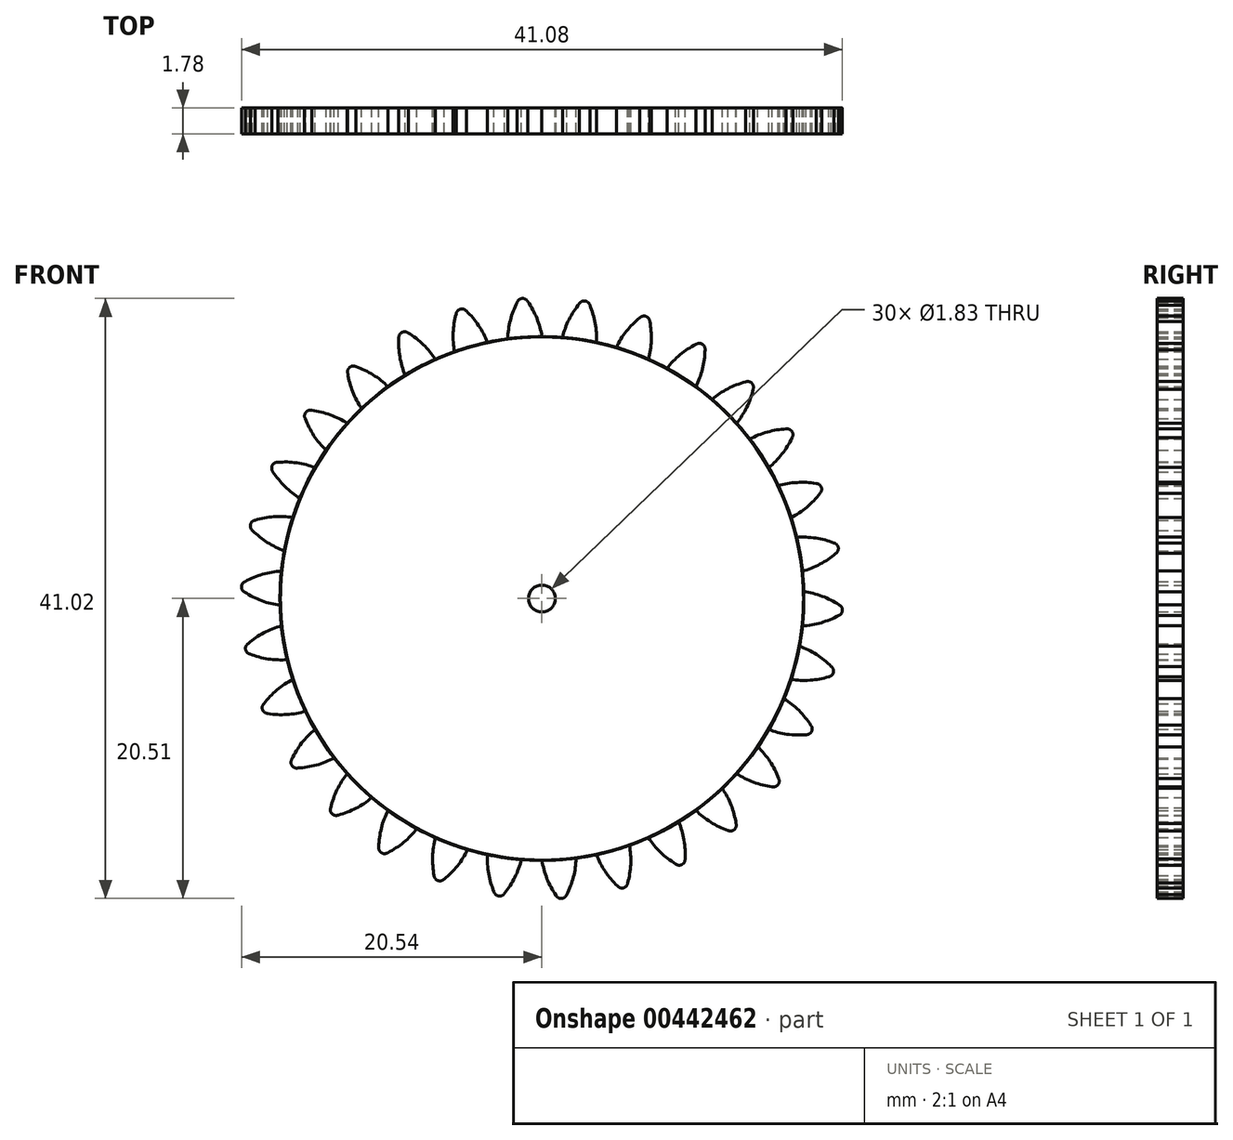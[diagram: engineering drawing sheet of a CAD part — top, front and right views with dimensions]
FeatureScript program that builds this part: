
annotation { "Feature Type Name" : "Feature", "Feature Type Description" : "" }
export const myFeature = defineFeature(function(context is Context, id is Id, definition is map)
    precondition{}
    {
        {
            var Q0;
            Q0=qCreatedBy(makeId("Front.planeOp"),FACE);
            var sketch = newSketch(context, id + "F0", { "sketchPlane" : qUnion([Q0])});
            skCircle(sketch, "E0", {"center": v(0, 0) * mm, "radius": 17.9 * mm});
            skCircle(sketch, "E1", {"center": v(0, 0) * mm, "radius": 19.05 * mm, "construction": true});
            skCircle(sketch, "E2", {"center": v(0, 0) * mm, "radius": 20.32 * mm, "construction": true});
            skLineSegment(sketch, "E3", {"start": v(0, 0) * mm, "end": v(0, 25.52) * mm, "construction": true});
            skLineSegment(sketch, "E4", {"start": v(0, 0) * mm, "end": v(-1.67, 25.47) * mm, "construction": true});
            skLineSegment(sketch, "E5", {"start": v(0, 19.05) * mm, "end": v(-25.53, 19.05) * mm, "construction": true});
            skLineSegment(sketch, "E6", {"start": v(0, 19.05) * mm, "end": v(-27.22, 9.14) * mm, "construction": true});
            skCircle(sketch, "E7", {"center": v(0, 19.05) * mm, "radius": 1.54 * mm, "construction": true});
            skCircle(sketch, "E8", {"center": v(-6.12, 16.82) * mm, "radius": 6.22 * mm, "construction": true});
            skArc(sketch, "E9", {"start": v(0, 17.9) * mm, "mid": v(-0.35, 19.15) * mm, "end": v(-0.97, 20.3) * mm});
            skArc(sketch, "E10.MirrorCS", {"start": v(-2.34, 17.75) * mm, "mid": v(-2.16, 19.04) * mm, "end": v(-1.7, 20.25) * mm});
            skArc(sketch, "E11", {"start": v(-0.97, 20.3) * mm, "mid": v(-1.34, 20.51) * mm, "end": v(-1.7, 20.25) * mm});
            skCircle(sketch, "E12", {"center": v(0, 0) * mm, "radius": 0.92 * mm});
            skSolve(sketch);
        }
        {
            var Q0;
            Q0 = qSketchRegion(id + "F0", true);
            extrude(context, id + "F1", {"entities" : qUnion([Q0]), "depth" : 1.78 * mm, "offsetDistance" : 25.4 * mm});
        }
        {
            var Q0;
            Q0=makeQuery(id+"F1.opExtrude","SWEPT_BODY",BODY,{"disambiguationData":[OSD([sQuery(id+"F0.wireOp",EDGE,"E0"),sQuery(id+"F0.wireOp",EDGE,"E9"),sQuery(id+"F0.wireOp",EDGE,"E10.MirrorCS"),sQuery(id+"F0.wireOp",EDGE,"E11")])]});
            var Q1;
            Q1=makeQuery(id+"F1.opExtrude","SWEPT_FACE",FACE,{"disambiguationData":[OSD([sQuery(id+"F0.wireOp",EDGE,"E0")])]});
            circularPattern(context, id + "F2", {"entities" : qUnion([Q0]), "axis" : qUnion([Q1]), "angle" : 360 * degree, "instanceCount" : 30, "equalSpace" : true});
        }
    });
